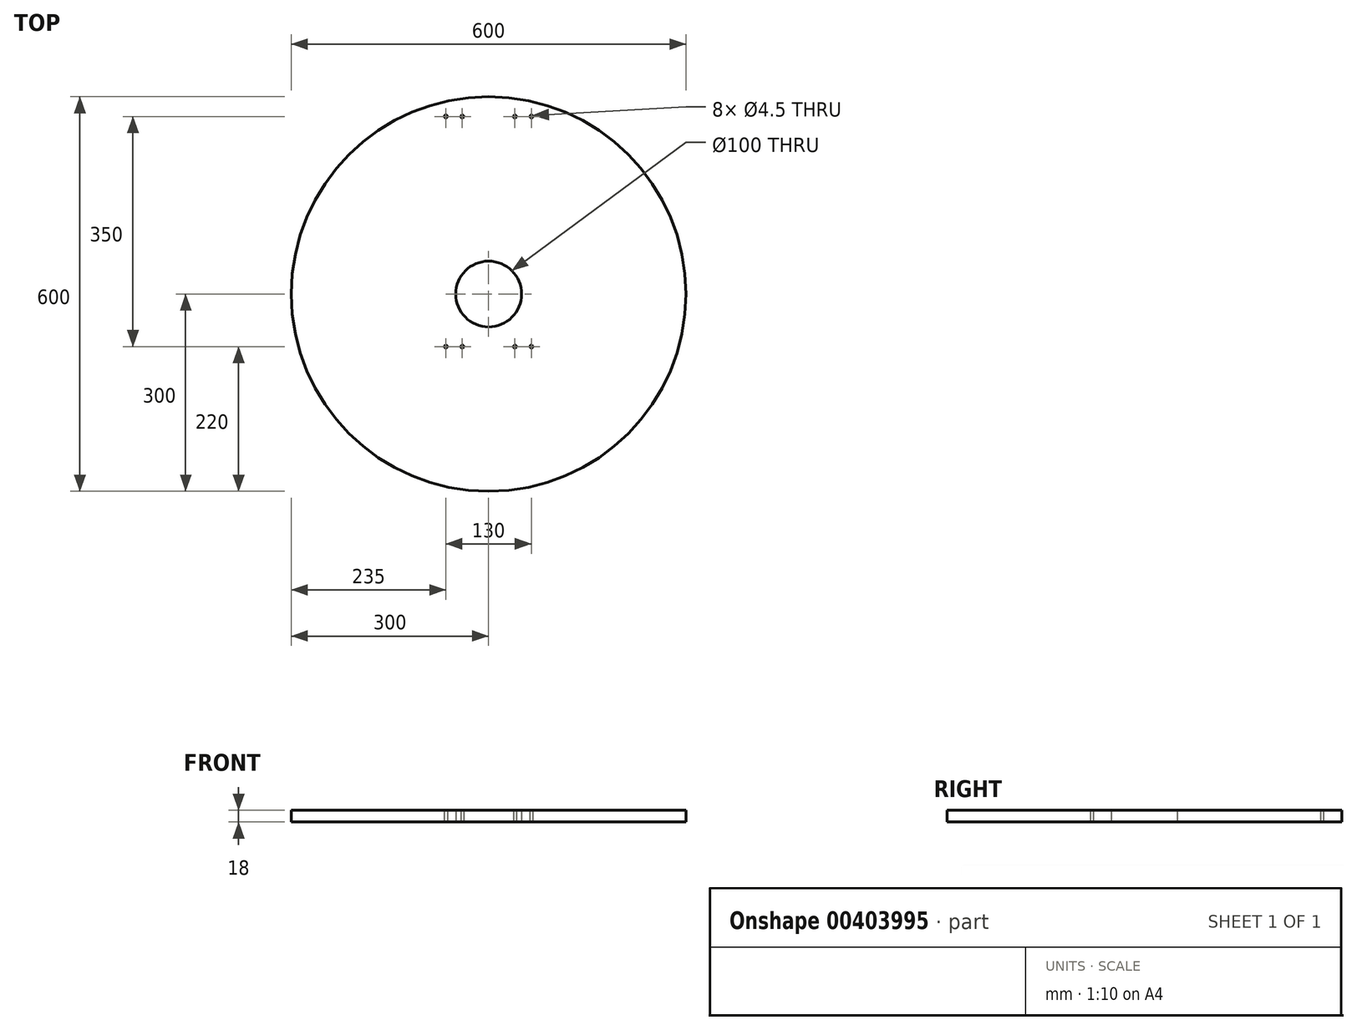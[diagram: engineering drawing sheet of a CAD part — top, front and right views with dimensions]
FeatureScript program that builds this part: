
annotation { "Feature Type Name" : "Feature", "Feature Type Description" : "" }
export const myFeature = defineFeature(function(context is Context, id is Id, definition is map)
    precondition{}
    {
        {
            var Q0;
            Q0=qCreatedBy(makeId("Top.planeOp"),FACE);
            var sketch = newSketch(context, id + "F0", { "sketchPlane" : qUnion([Q0])});
            skCircle(sketch, "E0", {"center": v(0, 0) * mm, "radius": 300 * mm});
            skCircle(sketch, "E1", {"center": v(0, 0) * mm, "radius": 50 * mm});
            skCircle(sketch, "E2", {"center": v(-65, -80) * mm, "radius": 2.25 * mm});
            skCircle(sketch, "E3", {"center": v(-40, -80) * mm, "radius": 2.25 * mm});
            skCircle(sketch, "E4", {"center": v(40, -80) * mm, "radius": 2.25 * mm});
            skCircle(sketch, "E5", {"center": v(65, -80) * mm, "radius": 2.25 * mm});
            skLineSegment(sketch, "E6", {"start": v(-65, -80) * mm, "end": v(65, -80) * mm, "construction": true});
            skLineSegment(sketch, "E7", {"start": v(0, 0) * mm, "end": v(0, -93.4) * mm, "construction": true});
            skLineSegment(sketch, "E8.0.1.0", {"start": v(-65, 270) * mm, "end": v(65, 270) * mm, "construction": true});
            skCircle(sketch, "E8.0.1.1", {"center": v(40, 270) * mm, "radius": 2.25 * mm});
            skCircle(sketch, "E8.0.1.2", {"center": v(-40, 270) * mm, "radius": 2.25 * mm});
            skCircle(sketch, "E8.0.1.3", {"center": v(65, 270) * mm, "radius": 2.25 * mm});
            skCircle(sketch, "E8.0.1.4", {"center": v(-65, 270) * mm, "radius": 2.25 * mm});
            skLineSegment(sketch, "E8.direction1", {"start": v(-65, -80) * mm, "end": v(-132, -80) * mm, "construction": true});
            skLineSegment(sketch, "E8.direction2", {"start": v(-65, -80) * mm, "end": v(-65, 270) * mm, "construction": true});
            skSolve(sketch);
        }
        {
            var Q0;
            Q0=makeQuery(id+"F0.imprint","IMPRINT",FACE,{"disambiguationData":[TD([[makeQuery(id+"F0.imprint","IMPRINT",EDGE,{"derivedFrom":sQuery(id+"F0.wireOp",EDGE,"E0")}),1.0]])]});
            extrude(context, id + "F1", {"entities" : qUnion([Q0]), "depth" : 18 * mm});
        }
    });
